# Revit family: Sink-Round Bowl-Clark Undermount1
name_source: partatom
category: Plumbing Fixtures
revit_build: Autodesk Revit Architecture 2012 (Build: 20110916_2132(x64)
units: mm (PartAtom-declared; Revit-internal decimal feet)

## types (1)
- Round Bowl
    Assembly Code = D2010410
    CW Connection = No
    Cost = 0 $
    Default Elevation = 0 mm  [stored 0 ft]
    Depth_ANZRS = 200 mm  [stored 0.656168 ft]
    Description = Round Bowl Undermount
    HW Connection = No
    Keynote = SK
    Length_ANZRS = 415 mm  [stored 1.36155 ft]
    Manufacturer = Clark
    Material_ANZRS = Metal-Stainless-Caroma
    Model = 4011
    Type Comments = Includes basket waste, Bowl Volume 22.5L, Carton size 450 x 510 x 210, Carton weight 2.8kg
    URL = http://www.clark.com.au
    Vent Connection = No
    WFU = 2
    Waste Connection = Yes
    Waste Radius = 25 mm  [stored 0.082021 ft]
    Width_ANZRS = 415 mm  [stored 1.36155 ft]

note: [stored X ft] marks values corroborated as IEEE doubles in the binary element streams (Revit-internal decimal feet)

## geometry (parser evidence)
native form markers: Blend x6, Sweep x2
no freeform markers — native parametric forms only
